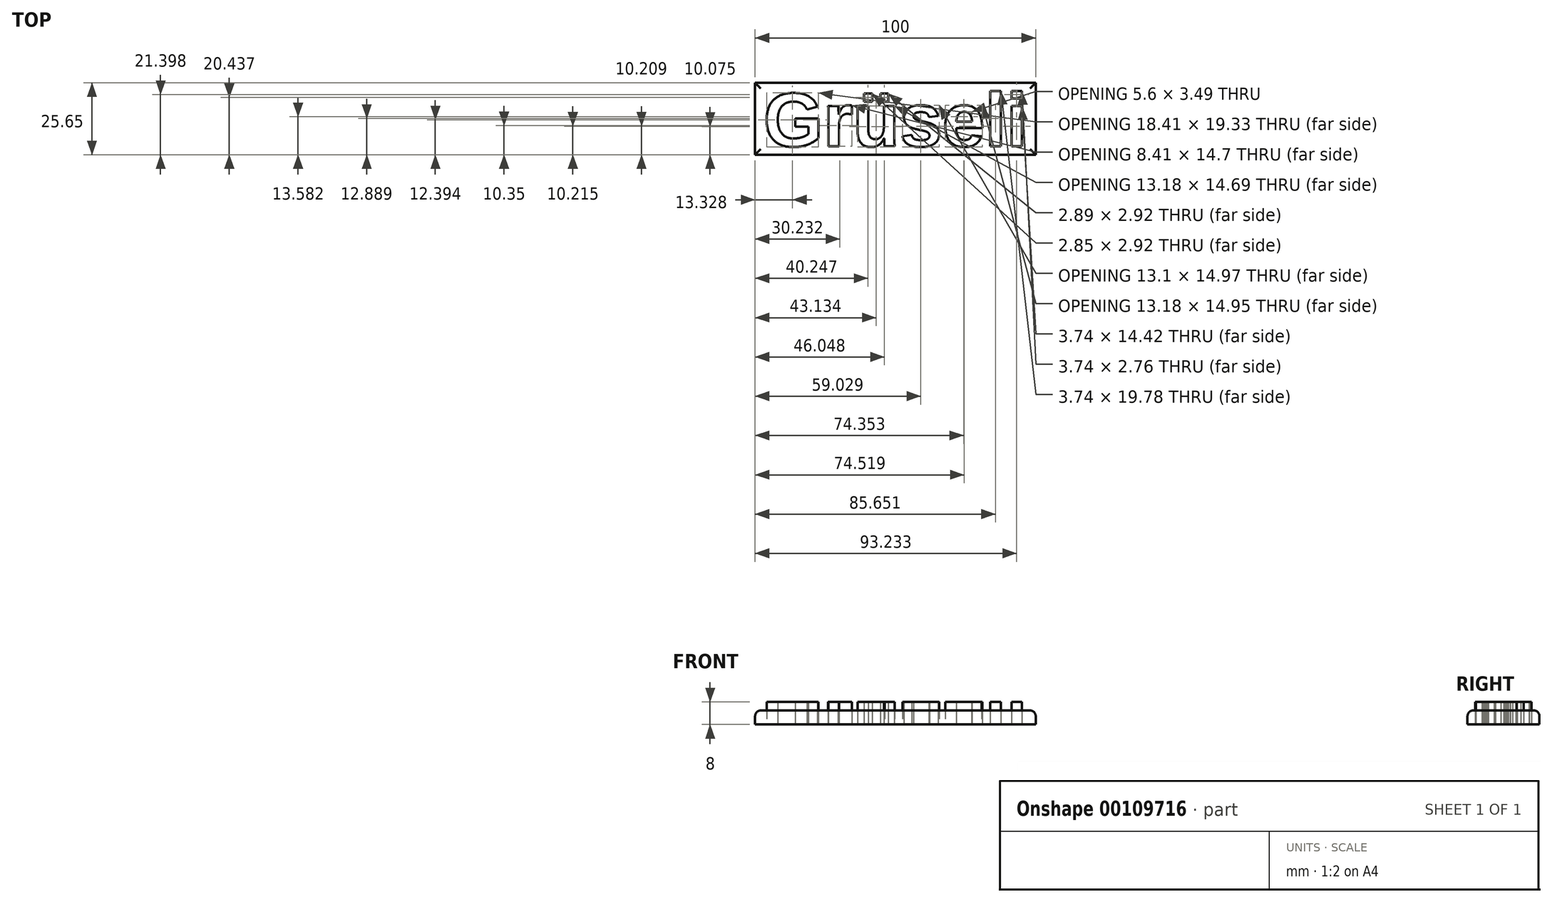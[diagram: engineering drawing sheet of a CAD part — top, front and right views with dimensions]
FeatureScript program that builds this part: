
annotation { "Feature Type Name" : "Feature", "Feature Type Description" : "" }
export const myFeature = defineFeature(function(context is Context, id is Id, definition is map)
    precondition{}
    {
        {
            var Q0;
            Q0=qCreatedBy(makeId("Top.planeOp"),FACE);
            var sketch = newSketch(context, id + "F0", { "sketchPlane" : qUnion([Q0])});
            skLineSegment(sketch, "E0.bottom", {"start": v(-51.25, 13.4) * mm, "end": v(48.75, 13.4) * mm});
            skLineSegment(sketch, "E0.top", {"start": v(-51.25, -12.24) * mm, "end": v(48.75, -12.24) * mm});
            skLineSegment(sketch, "E0.left", {"start": v(-51.25, 13.4) * mm, "end": v(-51.25, -12.24) * mm});
            skLineSegment(sketch, "E0.right", {"start": v(48.75, 13.4) * mm, "end": v(48.75, -12.24) * mm});
            skText(sketch, "E1", { "text": "Grüseli", "fontName": "Arimo-Bold.ttf"});
            const initialGuessF0  = {"E1": [-0.04825, -0.00924, 1, 0, 0.01965]};
            skSetInitialGuess(sketch, initialGuessF0);
            skSolve(sketch);
        }
        {
            var Q0;
            Q0=makeQuery(id+"F0.imprint","IMPRINT",FACE,{"disambiguationData":[TD([[makeQuery(id+"F0.imprint","IMPRINT",EDGE,{"derivedFrom":sQuery(id+"F0.wireOp",EDGE,"E0.bottom")}),-1.0]])]});
            var Q1;
            Q1=makeQuery(id+"F0.imprint","IMPRINT",FACE,{"disambiguationData":[TD([[makeQuery(id+"F0.imprint","IMPRINT",EDGE,{"derivedFrom":sQuery(id+"F0.wireOp",EDGE,"E1.sketch_text.stroke-105")}),1.0]])]});
            extrude(context, id + "F1", {"entities" : qUnion([Q0, Q1]), "depth" : 5 * mm});
        }
        {
            var Q0;
            Q0=makeQuery(id+"F0.imprint","IMPRINT",FACE,{"disambiguationData":[TD([[makeQuery(id+"F0.imprint","IMPRINT",EDGE,{"derivedFrom":sQuery(id+"F0.wireOp",EDGE,"E1.sketch_text.stroke-0")}),-1.0]])]});
            var Q1;
            Q1=makeQuery(id+"F0.imprint","IMPRINT",FACE,{"disambiguationData":[TD([[makeQuery(id+"F0.imprint","IMPRINT",EDGE,{"derivedFrom":sQuery(id+"F0.wireOp",EDGE,"E1.sketch_text.stroke-21")}),-1.0]])]});
            var Q2;
            Q2=makeQuery(id+"F0.imprint","IMPRINT",FACE,{"disambiguationData":[TD([[makeQuery(id+"F0.imprint","IMPRINT",EDGE,{"derivedFrom":sQuery(id+"F0.wireOp",EDGE,"E1.sketch_text.stroke-38")}),-1.0]])]});
            var Q3;
            Q3=makeQuery(id+"F0.imprint","IMPRINT",FACE,{"disambiguationData":[TD([[makeQuery(id+"F0.imprint","IMPRINT",EDGE,{"derivedFrom":sQuery(id+"F0.wireOp",EDGE,"E1.sketch_text.stroke-59")}),-1.0]])]});
            var Q4;
            Q4=makeQuery(id+"F0.imprint","IMPRINT",FACE,{"disambiguationData":[TD([[makeQuery(id+"F0.imprint","IMPRINT",EDGE,{"derivedFrom":sQuery(id+"F0.wireOp",EDGE,"E1.sketch_text.stroke-55")}),-1.0]])]});
            var Q5;
            Q5=makeQuery(id+"F0.imprint","IMPRINT",FACE,{"disambiguationData":[TD([[makeQuery(id+"F0.imprint","IMPRINT",EDGE,{"derivedFrom":sQuery(id+"F0.wireOp",EDGE,"E1.sketch_text.stroke-63")}),-1.0]])]});
            var Q6;
            Q6=makeQuery(id+"F0.imprint","IMPRINT",FACE,{"disambiguationData":[TD([[makeQuery(id+"F0.imprint","IMPRINT",EDGE,{"derivedFrom":sQuery(id+"F0.wireOp",EDGE,"E1.sketch_text.stroke-92")}),-1.0]])]});
            var Q7;
            Q7=makeQuery(id+"F0.imprint","IMPRINT",FACE,{"disambiguationData":[TD([[makeQuery(id+"F0.imprint","IMPRINT",EDGE,{"derivedFrom":sQuery(id+"F0.wireOp",EDGE,"E1.sketch_text.stroke-110")}),-1.0]])]});
            var Q8;
            Q8=makeQuery(id+"F0.imprint","IMPRINT",FACE,{"disambiguationData":[TD([[makeQuery(id+"F0.imprint","IMPRINT",EDGE,{"derivedFrom":sQuery(id+"F0.wireOp",EDGE,"E1.sketch_text.stroke-114")}),-1.0]])]});
            var Q9;
            Q9=makeQuery(id+"F0.imprint","IMPRINT",FACE,{"disambiguationData":[TD([[makeQuery(id+"F0.imprint","IMPRINT",EDGE,{"derivedFrom":sQuery(id+"F0.wireOp",EDGE,"E1.sketch_text.stroke-118")}),-1.0]])]});
            extrude(context, id + "F2", {"entities" : qUnion([Q0, Q1, Q2, Q3, Q4, Q5, Q6, Q7, Q8, Q9]), "depth" : 8 * mm});
        }
        {
            var Q0;
            Q0=makeQuery(id+"F1.opExtrude","CAP_EDGE",EDGE,{"disambiguationData":[OSD([sQuery(id+"F0.wireOp",EDGE,"E0.bottom")])],"isStart":false});
            var Q1;
            Q1=makeQuery(id+"F1.opExtrude","CAP_EDGE",EDGE,{"disambiguationData":[OSD([sQuery(id+"F0.wireOp",EDGE,"E0.left")])],"isStart":false});
            var Q2;
            Q2=makeQuery(id+"F1.opExtrude","CAP_EDGE",EDGE,{"disambiguationData":[OSD([sQuery(id+"F0.wireOp",EDGE,"E0.top")])],"isStart":false});
            var Q3;
            Q3=makeQuery(id+"F1.opExtrude","CAP_EDGE",EDGE,{"disambiguationData":[OSD([sQuery(id+"F0.wireOp",EDGE,"E0.right")])],"isStart":false});
            fillet(context, id + "F3", {"entities" : qUnion([Q0, Q1, Q2, Q3]), "radius" : 2 * mm, "tangentPropagation" : true, "allowEdgeOverflow" : false});
        }
    });
